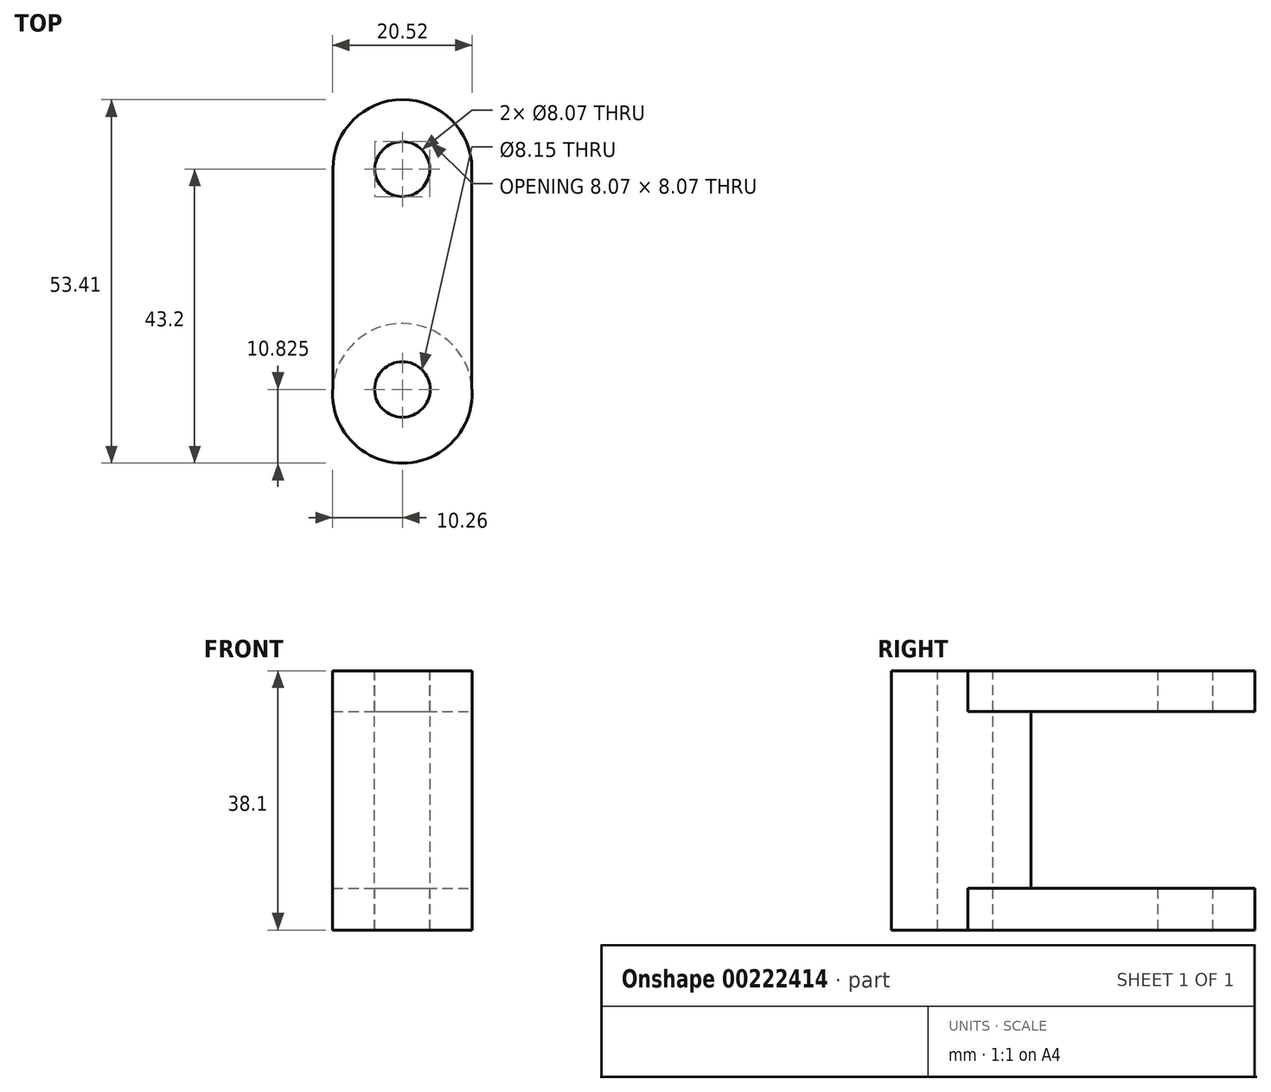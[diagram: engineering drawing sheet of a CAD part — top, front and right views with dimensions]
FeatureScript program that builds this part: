
annotation { "Feature Type Name" : "Feature", "Feature Type Description" : "" }
export const myFeature = defineFeature(function(context is Context, id is Id, definition is map)
    precondition{}
    {
        {
            var Q0;
            Q0=qCreatedBy(makeId("Top.planeOp"),FACE);
            var sketch = newSketch(context, id + "F0", { "sketchPlane" : qUnion([Q0])});
            skLineSegment(sketch, "E0.bottom", {"start": v(-10.21, 0) * mm, "end": v(10.21, 0) * mm});
            skLineSegment(sketch, "E0.top", {"start": v(-10.21, -32.96) * mm, "end": v(10.21, -32.96) * mm});
            skLineSegment(sketch, "E0.left", {"start": v(-10.21, 0) * mm, "end": v(-10.21, -32.96) * mm});
            skLineSegment(sketch, "E0.right", {"start": v(10.21, 0) * mm, "end": v(10.21, -32.96) * mm});
            skArc(sketch, "E1", {"start": v(10.21, 0) * mm, "mid": v(0, 10.21) * mm, "end": v(-10.21, 0) * mm});
            skArc(sketch, "E2", {"start": v(-10.21, -32.96) * mm, "mid": v(0, -43.18) * mm, "end": v(10.21, -32.96) * mm});
            skSolve(sketch);
        }
        {
            var Q0;
            Q0 = qSketchRegion(id + "F0", true);
            extrude(context, id + "F1", {"entities" : qUnion([Q0]), "depth" : 38.1 * mm});
        }
        {
            var Q0;
            Q0=makeQuery(id+"F1.opExtrude","CAP_FACE",FACE,{"disambiguationData":[OSD([sQuery(id+"F0.wireOp",EDGE,"E0.left"),sQuery(id+"F0.wireOp",EDGE,"E0.right"),sQuery(id+"F0.wireOp",EDGE,"E1"),sQuery(id+"F0.wireOp",EDGE,"E2")])],"isStart":false});
            var sketch = newSketch(context, id + "F2", { "sketchPlane" : qUnion([Q0])});
            skCircle(sketch, "E3", {"center": v(0, -32.96) * mm, "radius": 4.02 * mm});
            skCircle(sketch, "E4", {"center": v(0, 0) * mm, "radius": 4.04 * mm});
            skSolve(sketch);
        }
        {
            var Q0;
            Q0=makeQuery(id+"F2.imprint","IMPRINT",FACE,{"disambiguationData":[TD([[makeQuery(id+"F2.imprint","IMPRINT",EDGE,{"derivedFrom":sQuery(id+"F2.wireOp",EDGE,"E4")}),1.0]])]});
            var Q1;
            Q1 = qSketchRegion(id + "FWy5HypEbdRWbnZ_1", true);
            extrude(context, id + "F3", {"entities" : qUnion([Q0, Q1]), "operationType" : NewBodyOperationType.REMOVE, "endBound" : BoundingType.THROUGH_ALL, "oppositeDirection" : true, "depth" : 25.4 * mm});
        }
        {
            var Q0;
            Q0=makeQuery(id+"F1.opExtrude","CAP_FACE",FACE,{"disambiguationData":[OSD([sQuery(id+"F0.wireOp",EDGE,"E0.left"),sQuery(id+"F0.wireOp",EDGE,"E0.right"),sQuery(id+"F0.wireOp",EDGE,"E1"),sQuery(id+"F0.wireOp",EDGE,"E2")])],"isStart":false});
            var sketch = newSketch(context, id + "F4", { "sketchPlane" : qUnion([Q0])});
            skSolve(sketch);
        }
        {
            var Q0;
            Q0=makeQuery(id+"F1.opExtrude","SWEPT_FACE",FACE,{"disambiguationData":[OSD([sQuery(id+"F0.wireOp",EDGE,"E0.left")])]});
            var sketch = newSketch(context, id + "F5", { "sketchPlane" : qUnion([Q0])});
            skLineSegment(sketch, "E5.bottom", {"start": v(-14.98, 6.14) * mm, "end": v(71.17, 6.14) * mm});
            skLineSegment(sketch, "E5.top", {"start": v(-14.98, 32.1) * mm, "end": v(71.17, 32.1) * mm});
            skLineSegment(sketch, "E5.left", {"start": v(-14.98, 6.14) * mm, "end": v(-14.98, 32.1) * mm});
            skLineSegment(sketch, "E5.right", {"start": v(71.17, 6.14) * mm, "end": v(71.17, 32.1) * mm});
            skSolve(sketch);
        }
        {
            var Q0;
            Q0 = qSketchRegion(id + "F5", true);
            extrude(context, id + "F6", {"entities" : qUnion([Q0]), "operationType" : NewBodyOperationType.REMOVE, "endBound" : BoundingType.THROUGH_ALL, "oppositeDirection" : true, "depth" : 25.4 * mm});
        }
        {
            var Q0;
            Q0=makeQuery(id+"F4.imprint","IMPRINT",FACE,{"disambiguationData":[TD([[makeQuery(id+"F4.imprint","IMPRINT",EDGE,{"derivedFrom":makeQuery(id+"F1.opExtrude","CAP_EDGE",EDGE,{"disambiguationData":[OSD([sQuery(id+"F0.wireOp",EDGE,"E0.left")])],"isStart":false})}),1.0]])]});
            var sketch = newSketch(context, id + "F7", { "sketchPlane" : qUnion([Q0])});
            skCircle(sketch, "E6", {"center": v(0, -32.95) * mm, "radius": 10.26 * mm});
            skSolve(sketch);
        }
        {
            var Q0;
            Q0 = qSketchRegion(id + "F7", true);
            extrude(context, id + "F8", {"entities" : qUnion([Q0]), "operationType" : NewBodyOperationType.ADD, "oppositeDirection" : true, "depth" : 38.1 * mm});
        }
        {
            var Q0;
            Q0=makeQuery(id+"F4.imprint","IMPRINT",FACE,{"disambiguationData":[TD([[makeQuery(id+"F4.imprint","IMPRINT",EDGE,{"derivedFrom":makeQuery(id+"F1.opExtrude","CAP_EDGE",EDGE,{"disambiguationData":[OSD([sQuery(id+"F0.wireOp",EDGE,"E0.left")])],"isStart":false})}),1.0]])]});
            var sketch = newSketch(context, id + "F9", { "sketchPlane" : qUnion([Q0])});
            skCircle(sketch, "E7", {"center": v(0, -32.37) * mm, "radius": 4.08 * mm});
            skSolve(sketch);
        }
        {
            var Q0;
            Q0 = qSketchRegion(id + "F9", true);
            extrude(context, id + "F10", {"entities" : qUnion([Q0]), "operationType" : NewBodyOperationType.REMOVE, "endBound" : BoundingType.THROUGH_ALL, "oppositeDirection" : true, "depth" : 25.4 * mm});
        }
    });
